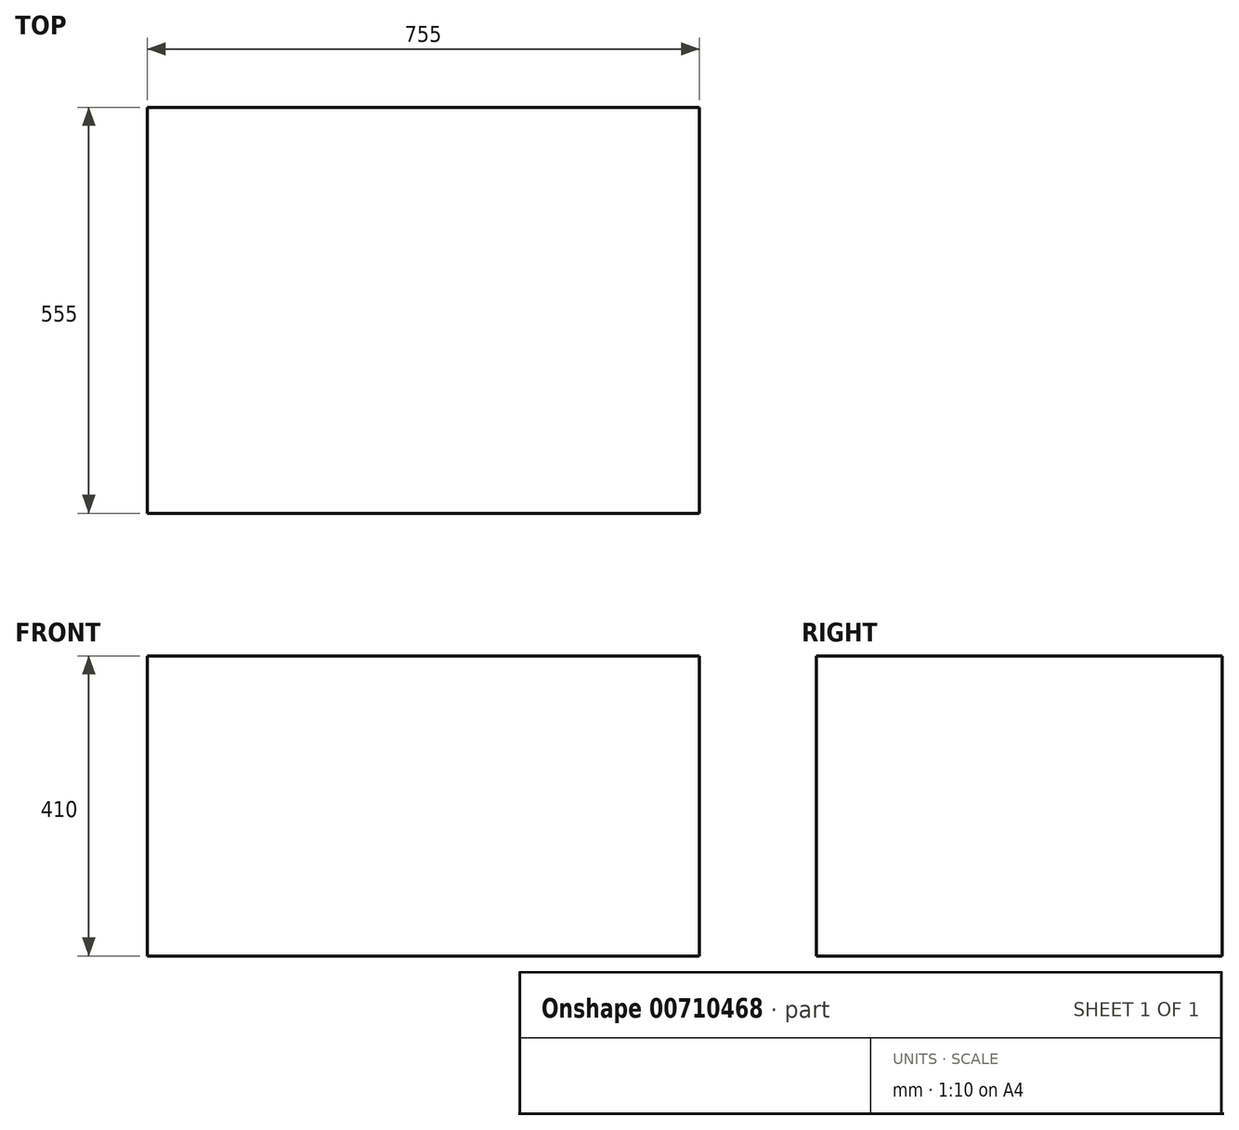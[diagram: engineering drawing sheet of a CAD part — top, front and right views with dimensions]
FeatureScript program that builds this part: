
annotation { "Feature Type Name" : "Feature", "Feature Type Description" : "" }
export const myFeature = defineFeature(function(context is Context, id is Id, definition is map)
    precondition{}
    {
        {
            var Q0;
            Q0=qCreatedBy(makeId("Top.planeOp"),FACE);
            var sketch = newSketch(context, id + "F0", { "sketchPlane" : qUnion([Q0])});
            skLineSegment(sketch, "E0.bottom", {"start": v(377.5, 277.5) * mm, "end": v(-377.5, 277.5) * mm});
            skLineSegment(sketch, "E0.top", {"start": v(377.5, -277.5) * mm, "end": v(-377.5, -277.5) * mm});
            skLineSegment(sketch, "E0.left", {"start": v(377.5, 277.5) * mm, "end": v(377.5, -277.5) * mm});
            skLineSegment(sketch, "E0.right", {"start": v(-377.5, 277.5) * mm, "end": v(-377.5, -277.5) * mm});
            skPoint(sketch, "E0.middle", {"position": v(0, 0) * mm});
            skSolve(sketch);
        }
        {
            var Q0;
            Q0 = qSketchRegion(id + "F0", true);
            extrude(context, id + "F1", {"entities" : qUnion([Q0]), "depth" : 410 * mm, "offsetDistance" : 25 * mm});
        }
    });
